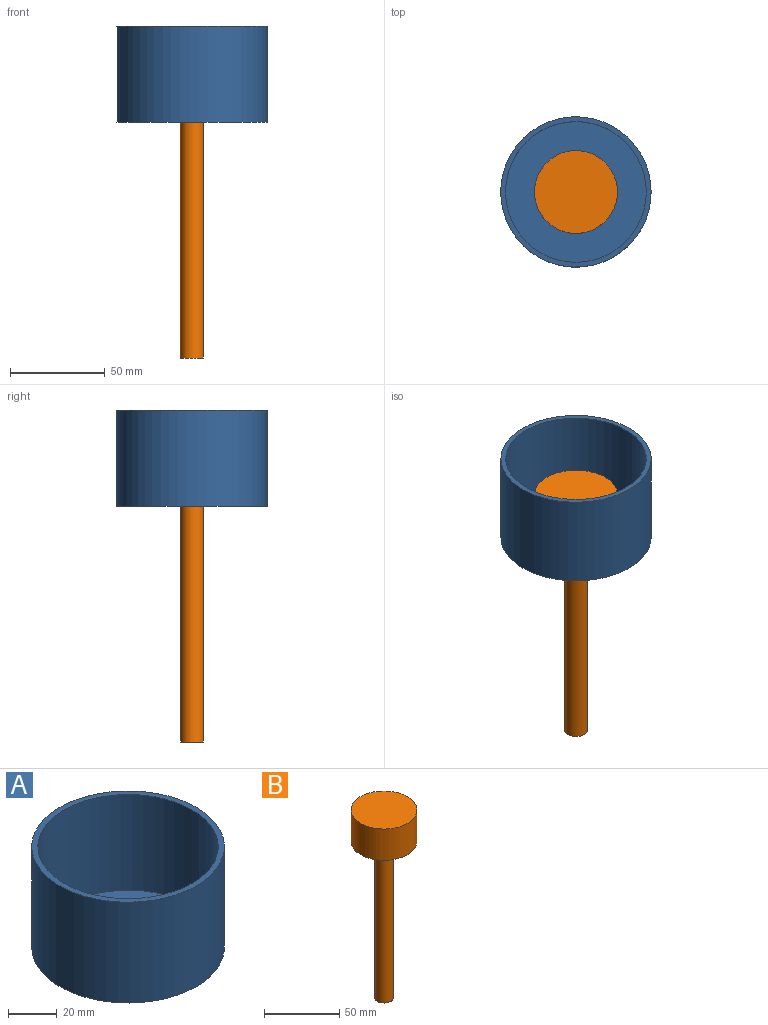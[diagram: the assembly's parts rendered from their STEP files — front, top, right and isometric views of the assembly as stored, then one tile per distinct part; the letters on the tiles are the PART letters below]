
ASSEMBLY  parts=2 mates=1
PART A: 6 faces, bbox 79.3x79.3x50.8 mm
  f0: cylinder r=39.67mm len=79.35mm, axis (0,0,-1), area 12663.6mm2, adj f1,f2
  f1: plane 79.35x79.35mm, normal (0,0,1), area 612.9mm2, adj f0,f3
  f2: plane 79.35x79.35mm, normal (0,0,-1), area 4818.5mm2, adj f0,f5
  f3: cylinder r=37.13mm len=74.27mm, axis (0,0,-1), area 11260.3mm2, adj f1,f4
  f4: plane 74.27x74.27mm, normal (0,0,1), area 4205.6mm2, adj f3,f5
  f5: cylinder r=6.35mm len=12.7mm, axis (0,0,-1), area 101.3mm2, adj f2,f4
PART B: 5 faces, bbox 43.7x43.7x152.4 mm
  f0: cylinder r=6.06mm len=127mm, axis (0,0,-1), area 4832.1mm2, adj f1,f4
  f1: plane 12.11x12.11mm, normal (0,0,-1), area 115.2mm2, adj f0
  f2: cylinder r=21.87mm len=43.74mm, axis (0,0,-1), area 3490.1mm2, adj f3,f4
  f3: plane 43.74x43.74mm, normal (0,0,1), area 1502.5mm2, adj f2
  f4: plane 43.74x43.74mm, normal (0,0,-1), area 1387.3mm2, adj f0,f2
PLACE A t=(27.58,-9.32,-0.01)mm
PLACE B t=(27.58,-9.32,-124.47)mm
MATE fastened B.f2 <-> A.f0  axis (0,0,-1) through (27.58,-9.32,2.53)mm
